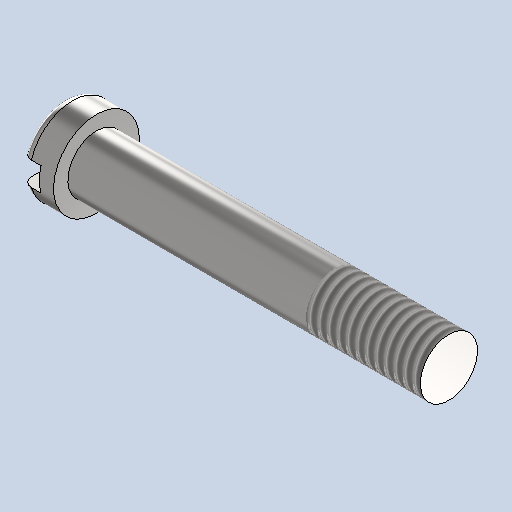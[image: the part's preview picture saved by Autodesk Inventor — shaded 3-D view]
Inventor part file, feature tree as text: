
AUTODESK INVENTOR PART (.ipt)
format: ipt  version: 2025 (Build 290162010, 162A)  size: 292,864 bytes
history: native  units: mm
features: sketch x2, revolve x1, thread x1, extrude x1, fillet x1
ambient origin geometry x8: Origin, YZ Plane, XZ Plane, XY Plane, X Axis, Y Axis, Z Axis, Center Point
bodies: Volumenkörper1 (feature_tree)
feature tree (6):
  revolve  "Umdrehung1"
  thread  "Gewinde1"  [1 undecoded]
  extrude  "Extrusion1"  Depth=9.0mm
  fillet  "Rundung1"  Radius=37.0mm
  sketch  "Skizze1"  dims[d1=6.0mm d2=9.0mm d3=37.0mm]
  sketch  "Skizze2"  dims[d4=90.0deg d5=12.0mm d6=0.0mm d7=2.5mm d8=2.0mm d9=0.0mm d10=1.0mm]
note: 1 required parameter value undecoded (feature->parameter linkage not recoverable at this tier; creation-order binding heuristic only, values carry confidence <= 0.55)
